# Revit family: Haworth_BuzziBracks_Worktop_Side_BUILD
name_source: partatom
category: Furniture
revit_build: Autodesk Revit 2018 (Build: 20170223_1515(x64)
units: mm (PartAtom-declared; Revit-internal decimal feet)

## family parameters
Always vertical = Yes
Cut with Voids When Loaded = No
OmniClass Number = 23.40.20.00
OmniClass Title = General Furniture and Specialties
Room Calculation Point = No
Shared = No
Work Plane-Based = No

## types (2) — shared parameters
Actual Depth = 29.5 "
Actual Height = 29.75 "
Assembly Code = E2020200
Cable Entry = Yes
Description = Haworth - BuzziBracks - Side Worktop
Manufacturer = Haworth
Model = HCBZ-BRW
Note = Verify Final Dim. w/ Haworth
Revision = 1
Thickness = 1.75 "
Top Radius = 4 "
URL = http://www.haworth.com
URL - Product = http://www.haworth.com
Void Dimension = 3 "
Warranty = http://www.haworth.com

## per-type parameters (varying)
| type | 29.5d x 44w | 29.5d x 56w | Actual Width |
| BRW - 44w Side Worktop - With Cable Entry | Yes | No | 44 " |
| BRW - 56w Side Worktop - With Cable Entry | No | Yes | 56 " |

## geometry (parser evidence)
native form markers: Sweep x2
no freeform markers — native parametric forms only
